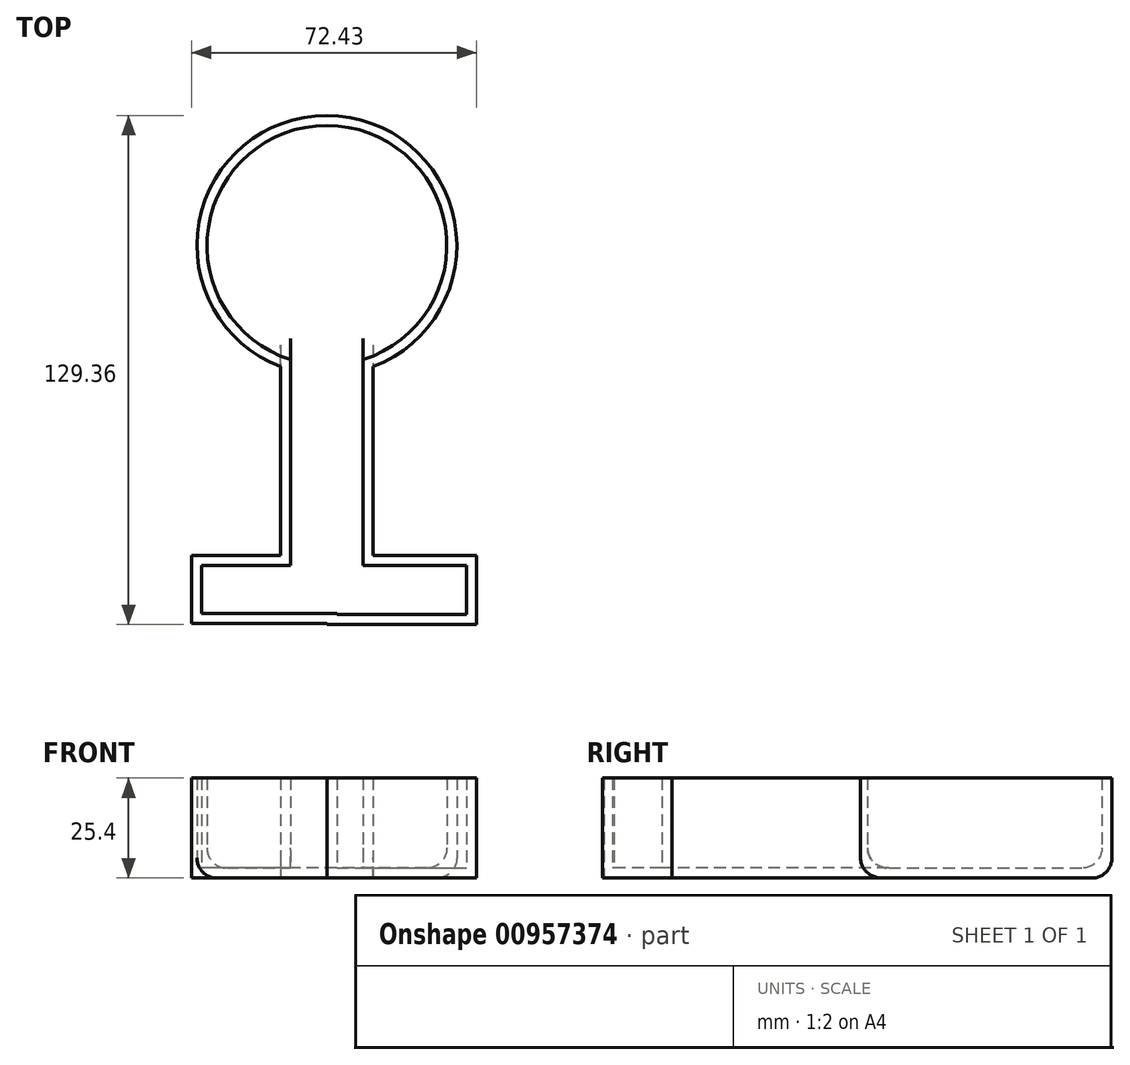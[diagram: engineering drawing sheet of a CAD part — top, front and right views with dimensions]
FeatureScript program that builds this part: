
annotation { "Feature Type Name" : "Feature", "Feature Type Description" : "" }
export const myFeature = defineFeature(function(context is Context, id is Id, definition is map)
    precondition{}
    {
        {
            var Q0;
            Q0=qCreatedBy(makeId("Top.planeOp"),FACE);
            var sketch = newSketch(context, id + "F0", { "sketchPlane" : qUnion([Q0])});
            skLineSegment(sketch, "E0.bottom", {"start": v(-49.83, -13.52) * mm, "end": v(-26.3, -13.52) * mm});
            skLineSegment(sketch, "E0.top", {"start": v(-49.83, -61.43) * mm, "end": v(-26.3, -61.43) * mm});
            skLineSegment(sketch, "E0.left", {"start": v(-49.83, -13.52) * mm, "end": v(-49.83, -61.43) * mm});
            skLineSegment(sketch, "E0.right", {"start": v(-26.3, -13.52) * mm, "end": v(-26.3, -61.43) * mm});
            skCircle(sketch, "E1", {"center": v(-38.06, 17.33) * mm, "radius": 33 * mm});
            skPoint(sketch, "E1.centerSnap0", {"position": v(-38.06, -13.52) * mm});
            skLineSegment(sketch, "E2.bottom", {"start": v(-38.06, -61.43) * mm, "end": v(-72.43, -61.43) * mm});
            skLineSegment(sketch, "E2.top", {"start": v(-38.06, -78.75) * mm, "end": v(-72.43, -78.75) * mm});
            skLineSegment(sketch, "E2.left", {"start": v(-38.06, -61.43) * mm, "end": v(-38.06, -78.75) * mm});
            skLineSegment(sketch, "E2.right", {"start": v(-72.43, -61.43) * mm, "end": v(-72.43, -78.75) * mm});
            skLineSegment(sketch, "E3.bottom", {"start": v(-38.06, -61.43) * mm, "end": v(0, -61.43) * mm});
            skLineSegment(sketch, "E3.top", {"start": v(-38.06, -79.03) * mm, "end": v(0, -79.03) * mm});
            skLineSegment(sketch, "E3.left", {"start": v(-38.06, -61.43) * mm, "end": v(-38.06, -79.03) * mm});
            skLineSegment(sketch, "E3.right", {"start": v(0, -61.43) * mm, "end": v(0, -79.03) * mm});
            skSolve(sketch);
        }
        {
            var Q0;
            {var subQ1=sQuery(id+"F0.wireOp",EDGE,"E0.left");Q0=makeQuery(id+"F0.imprint","IMPRINT",FACE,{"disambiguationData":[TD([[makeQuery(id+"F0.imprint","IMPRINT",EDGE,{"derivedFrom":subQ1}),1.0]])]});}
            var Q1;
            {var subQ0=sQuery(id+"F0.wireOp",EDGE,"E0.bottom");Q1=makeQuery(id+"F0.imprint","IMPRINT",FACE,{"disambiguationData":[TD([[makeQuery(id+"F0.imprint","IMPRINT",EDGE,{"derivedFrom":subQ0}),-1.0]])]});}
            var Q2;
            {var subQ0=sQuery(id+"F0.wireOp",EDGE,"E0.bottom");Q2=makeQuery(id+"F0.imprint","IMPRINT",FACE,{"disambiguationData":[TD([[makeQuery(id+"F0.imprint","IMPRINT",EDGE,{"derivedFrom":subQ0}),1.0]])]});}
            var Q3;
            {var subQ1=sQuery(id+"F0.wireOp",EDGE,"E2.top");Q3=makeQuery(id+"F0.imprint","IMPRINT",FACE,{"disambiguationData":[TD([[makeQuery(id+"F0.imprint","IMPRINT",EDGE,{"derivedFrom":subQ1}),-1.0]])]});}
            var Q4;
            {var subQ4=sQuery(id+"F0.wireOp",EDGE,"E3.top");Q4=makeQuery(id+"F0.imprint","IMPRINT",FACE,{"disambiguationData":[TD([[makeQuery(id+"F0.imprint","IMPRINT",EDGE,{"derivedFrom":subQ4}),1.0]])]});}
            extrude(context, id + "F1", {"entities" : qUnion([Q0, Q1, Q2, Q3, Q4]), "depth" : 25.4 * mm, "offsetDistance" : 25.4 * mm});
        }
        {
            var Q0;
            Q0=makeQuery(id+"F1.opExtrude","CAP_FACE",FACE,{"disambiguationData":[OSD([sQuery(id+"F0.wireOp",EDGE,"E0.left"),sQuery(id+"F0.wireOp",EDGE,"E0.right"),sQuery(id+"F0.wireOp",EDGE,"E1"),sQuery(id+"F0.wireOp",EDGE,"E2.bottom"),sQuery(id+"F0.wireOp",EDGE,"E2.top"),sQuery(id+"F0.wireOp",EDGE,"E2.right"),sQuery(id+"F0.wireOp",EDGE,"E3.bottom"),sQuery(id+"F0.wireOp",EDGE,"E3.top"),sQuery(id+"F0.wireOp",EDGE,"E3.left"),sQuery(id+"F0.wireOp",EDGE,"E3.right")])],"isStart":false});
            shell(context, id + "F2", {"entities" : qUnion([Q0]), "thickness" : 2.54 * mm});
        }
        {
            var Q0;
            {var subQ0=sQuery(id+"F0.wireOp",EDGE,"E1");Q0=makeQuery(id+"F2.opShell","OFFSET_EDGE",EDGE,{"disambiguationData":[OSD([subQ0]),TDD([makeQuery(id+"F1.opExtrude","CAP_EDGE",EDGE,{"disambiguationData":[OSD([subQ0])],"isStart":true})])]});}
            var Q1;
            Q1=makeQuery(id+"F1.opExtrude","CAP_EDGE",EDGE,{"disambiguationData":[OSD([sQuery(id+"F0.wireOp",EDGE,"E1")])],"isStart":true});
            fillet(context, id + "F3", {"entities" : qUnion([Q0, Q1]), "radius" : 5.08 * mm, "tangentPropagation" : true, "allowEdgeOverflow" : false});
        }
    });
